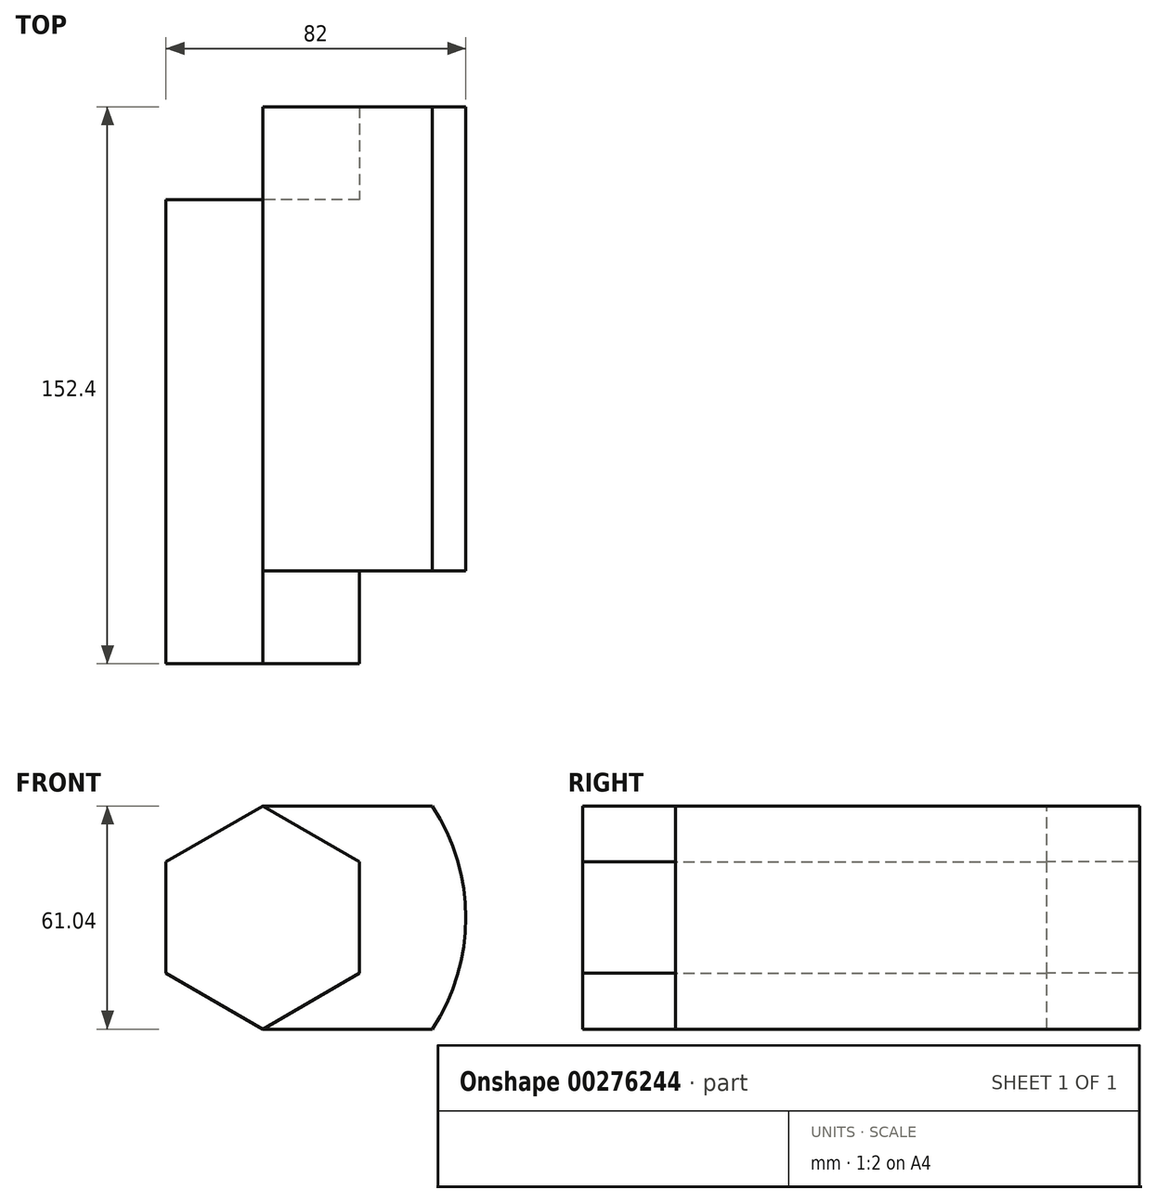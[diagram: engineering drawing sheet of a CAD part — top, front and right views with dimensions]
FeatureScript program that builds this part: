
annotation { "Feature Type Name" : "Feature", "Feature Type Description" : "" }
export const myFeature = defineFeature(function(context is Context, id is Id, definition is map)
    precondition{}
    {
        {
            var Q0;
            Q0=qCreatedBy(makeId("Front.planeOp"),FACE);
            var sketch = newSketch(context, id + "F0", { "sketchPlane" : qUnion([Q0])});
            skCircle(sketch, "E0.cCircle", {"center": v(-26.43, 20.71) * mm, "radius": 26.43 * mm, "construction": true});
            skLineSegment(sketch, "E0.0", {"start": v(0, 35.97) * mm, "end": v(0, 5.45) * mm});
            skLineSegment(sketch, "E0.1", {"start": v(0, 5.45) * mm, "end": v(-26.43, -9.8) * mm});
            skLineSegment(sketch, "E0.2", {"start": v(-26.43, -9.8) * mm, "end": v(-52.86, 5.45) * mm});
            skLineSegment(sketch, "E0.3", {"start": v(-52.86, 5.45) * mm, "end": v(-52.86, 35.97) * mm});
            skLineSegment(sketch, "E0.4", {"start": v(-52.86, 35.97) * mm, "end": v(-26.43, 51.23) * mm});
            skLineSegment(sketch, "E0.5", {"start": v(-26.43, 51.23) * mm, "end": v(0, 35.97) * mm});
            skPoint(sketch, "E0.0.midPoint", {"position": v(0, 20.71) * mm});
            skCircle(sketch, "E1", {"center": v(-26.43, 20.71) * mm, "radius": 55.57 * mm});
            skLineSegment(sketch, "E2", {"start": v(-26.43, 51.23) * mm, "end": v(21.36, 51.23) * mm});
            skLineSegment(sketch, "E3", {"start": v(20.73, 50.12) * mm, "end": v(21.36, 51.23) * mm});
            skLineSegment(sketch, "E4", {"start": v(-26.43, -9.8) * mm, "end": v(20.01, -9.8) * mm});
            skSolve(sketch);
        }
        {
            var Q0;
            Q0=makeQuery(id+"F0.imprint","IMPRINT",FACE,{"disambiguationData":[TD([[makeQuery(id+"F0.imprint","IMPRINT",EDGE,{"derivedFrom":sQuery(id+"F0.wireOp",EDGE,"E0.0")}),-1.0]])]});
            extrude(context, id + "F1", {"entities" : qUnion([Q0]), "depth" : 25.4 * mm});
        }
        {
            var Q0;
            Q0=makeQuery(id+"F0.imprint","IMPRINT",FACE,{"disambiguationData":[TD([[makeQuery(id+"F0.imprint","IMPRINT",EDGE,{"derivedFrom":sQuery(id+"F0.wireOp",EDGE,"E0.0")}),1.0]])]});
            var Q1;
            Q1=makeQuery(id+"F1.opExtrude","CAP_FACE",FACE,{"disambiguationData":[OSD([sQuery(id+"F0.wireOp",EDGE,"E0.0"),sQuery(id+"F0.wireOp",EDGE,"E0.1"),sQuery(id+"F0.wireOp",EDGE,"E0.2"),sQuery(id+"F0.wireOp",EDGE,"E0.3"),sQuery(id+"F0.wireOp",EDGE,"E0.4"),sQuery(id+"F0.wireOp",EDGE,"E0.5")])],"isStart":false});
            extrude(context, id + "F2", {"entities" : qUnion([Q0, Q1]), "operationType" : NewBodyOperationType.ADD, "oppositeDirection" : true, "depth" : 127 * mm});
        }
    });
